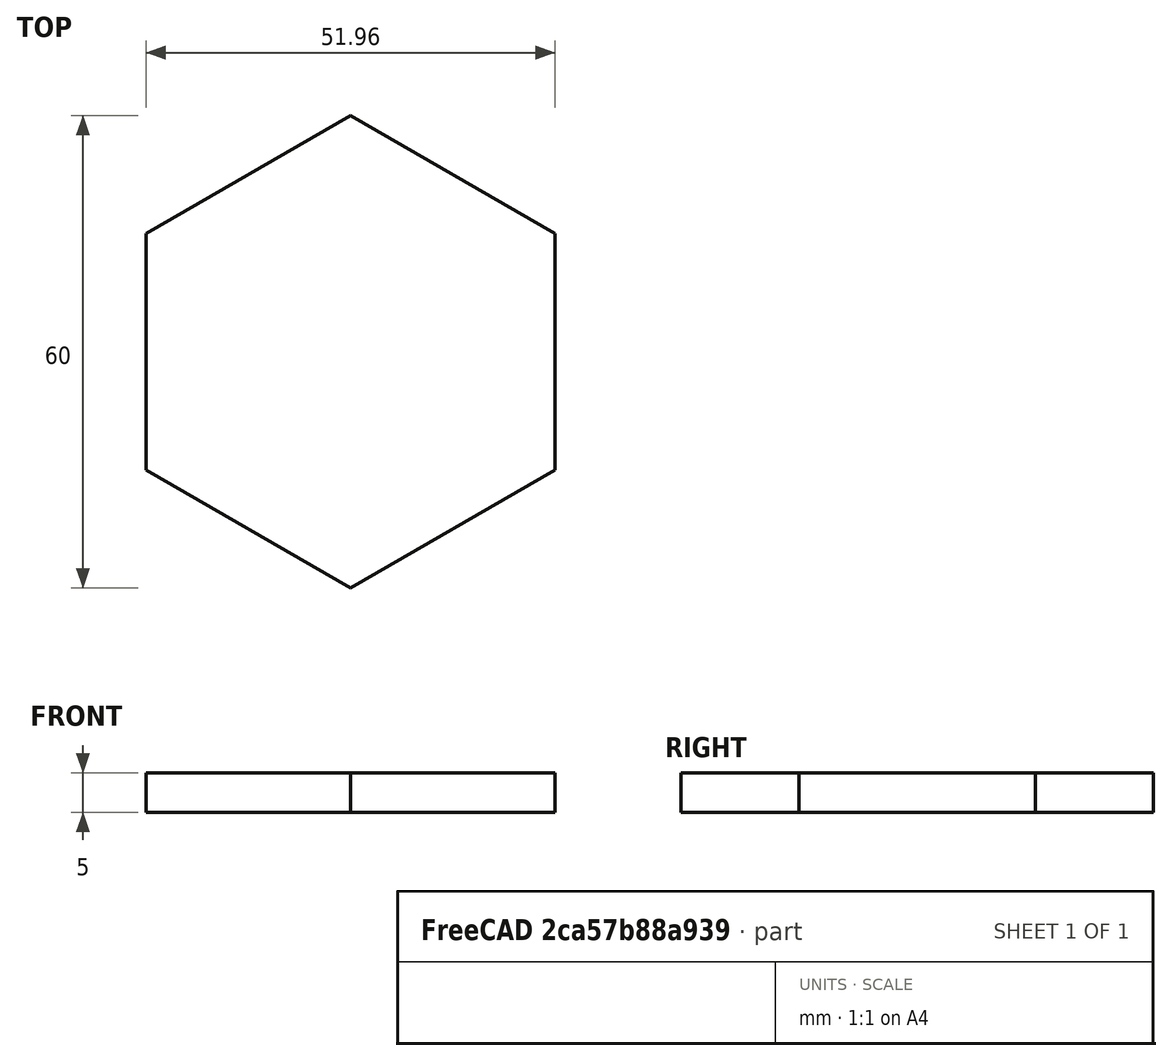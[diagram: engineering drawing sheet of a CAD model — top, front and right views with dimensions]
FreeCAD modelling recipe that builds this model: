
FCSTD DOCUMENT  (FreeCAD 0.19R)
Label: BodyTest_Minimal
License: Creative Commons Attribution-ShareAlike
LicenseURL: http://creativecommons.org/licenses/by-sa/4.0/
objects: Sketcher::SketchObject×1, PartDesign::Pad×1, PartDesign::Body×1
note: 4 computed .brp shape members not serialized (recipe doc carries the construction recipe); baked Part::Feature solids carry a one-line shape summary decoded from their .brp

FEATURE [Sketcher::SketchObject] Sketch
  MapMode = 5
  Support = -> [XY_Plane001]
  sketch-geometry (7):
    g0: LineSegment StartX=25.9808 StartY=15 StartZ=0 EndX=3.6e-15 EndY=30 EndZ=0
    g1: LineSegment StartX=2e-15 StartY=30 StartZ=0 EndX=-25.9808 EndY=15 EndZ=0
    g2: LineSegment StartX=-25.9808 StartY=15 StartZ=0 EndX=-25.9808 EndY=-15 EndZ=0
    g3: LineSegment StartX=-25.9808 StartY=-15 StartZ=0 EndX=0 EndY=-30 EndZ=0
    g4: LineSegment StartX=0 StartY=-30 StartZ=0 EndX=25.9808 EndY=-15 EndZ=0
    g5: LineSegment StartX=25.9808 StartY=-15 StartZ=0 EndX=25.9808 EndY=15 EndZ=0
    g6: Circle [constr] CenterX=0 CenterY=0 CenterZ=0 NormalX=0 NormalY=0 NormalZ=1 AngleXU=0 Radius=30
  constraints (16):
    c: Coincident(g0,g1)
    c: Coincident(g1,g2)
    c: Coincident(g2,g3)
    c: Coincident(g3,g4)
    c: Coincident(g4,g5)
    c: Coincident(g5,g0)
    c: Equal(g0, g1-g5) x5
    c: PointOnObject(g0,g6)
    c: PointOnObject(g1,g6)
    c: PointOnObject(g2,g6)
    c: PointOnObject(g3,g6)
    c: PointOnObject(g4,g6)
    c: PointOnObject(g5,g6)
    c: Coincident(g6,g-1)
    c: Vertical(g5)
    c: Radius(g6) = 30
FEATURE [PartDesign::Pad] Pad
  Length = 5
  Length2 = 100
  Profile = -> Sketch
  Type = 0
FEATURE [PartDesign::Body] Body  label="Body_Hex"
  Group = -> [Sketch,Pad]
  Origin = -> Origin001
  Tip = -> Pad
